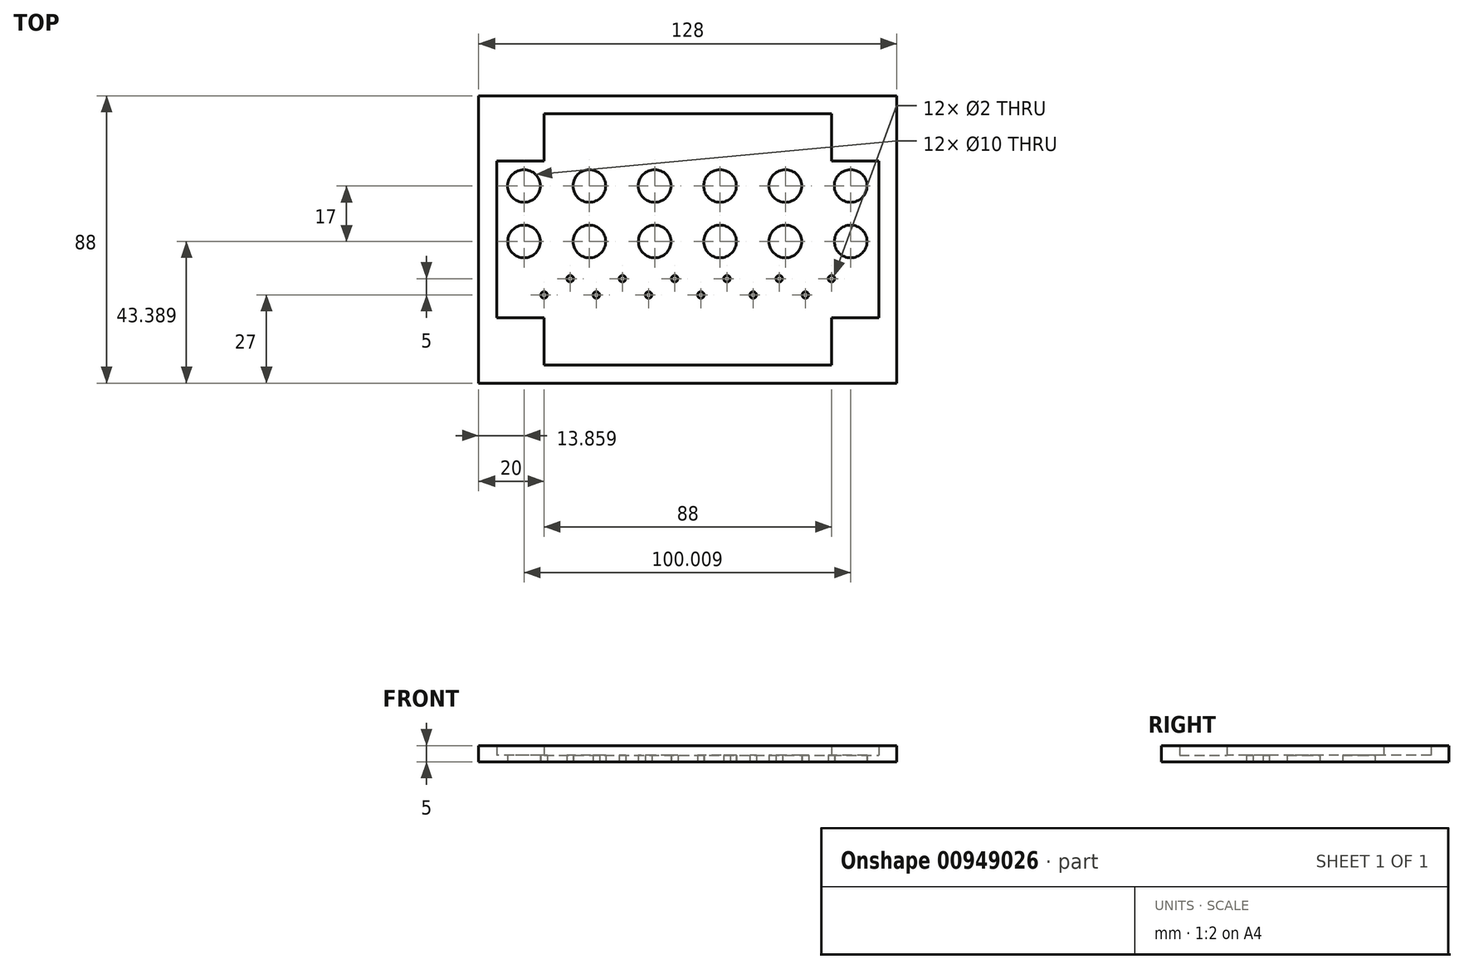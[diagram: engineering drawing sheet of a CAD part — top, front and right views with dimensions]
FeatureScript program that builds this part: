
annotation { "Feature Type Name" : "Feature", "Feature Type Description" : "" }
export const myFeature = defineFeature(function(context is Context, id is Id, definition is map)
    precondition{}
    {
        {
            var Q0;
            Q0=qCreatedBy(makeId("Top.planeOp"),FACE);
            var sketch = newSketch(context, id + "F0", { "sketchPlane" : qUnion([Q0])});
            skLineSegment(sketch, "E0.bottom", {"start": v(-64, 44) * mm, "end": v(64, 44) * mm});
            skLineSegment(sketch, "E0.top", {"start": v(-64, -44) * mm, "end": v(64, -44) * mm});
            skLineSegment(sketch, "E0.left", {"start": v(-64, 44) * mm, "end": v(-64, -44) * mm});
            skLineSegment(sketch, "E0.right", {"start": v(64, 44) * mm, "end": v(64, -44) * mm});
            skPoint(sketch, "E0.middle", {"position": v(0, 0) * mm});
            skLineSegment(sketch, "E1.bottom", {"start": v(-58.5, 38.5) * mm, "end": v(58.5, 38.5) * mm, "construction": true});
            skLineSegment(sketch, "E1.top", {"start": v(-58.5, -38.5) * mm, "end": v(58.5, -38.5) * mm, "construction": true});
            skLineSegment(sketch, "E1.left", {"start": v(-58.5, 38.5) * mm, "end": v(-58.5, -38.5) * mm, "construction": true});
            skLineSegment(sketch, "E1.right", {"start": v(58.5, 38.5) * mm, "end": v(58.5, -38.5) * mm, "construction": true});
            skLineSegment(sketch, "E2", {"start": v(44, 44) * mm, "end": v(44, 24) * mm, "construction": true});
            skLineSegment(sketch, "E3", {"start": v(44, 24) * mm, "end": v(64, 24) * mm, "construction": true});
            skLineSegment(sketch, "E4.MirrorCS", {"start": v(-44, 44) * mm, "end": v(-44, 24) * mm, "construction": true});
            skLineSegment(sketch, "E5.MirrorCS", {"start": v(-44, 24) * mm, "end": v(-64, 24) * mm, "construction": true});
            skLineSegment(sketch, "E6.MirrorCS", {"start": v(-44, -44) * mm, "end": v(-44, -24) * mm, "construction": true});
            skLineSegment(sketch, "E7.MirrorCS", {"start": v(-44, -24) * mm, "end": v(-64, -24) * mm, "construction": true});
            skLineSegment(sketch, "E8.MirrorCS", {"start": v(44, -44) * mm, "end": v(44, -24) * mm, "construction": true});
            skLineSegment(sketch, "E9.MirrorCS", {"start": v(44, -24) * mm, "end": v(64, -24) * mm, "construction": true});
            skLineSegment(sketch, "E10", {"start": v(-67.74, -17) * mm, "end": v(88.46, -17) * mm, "construction": true});
            skLineSegment(sketch, "E11", {"start": v(-79.12, -12) * mm, "end": v(91.25, -12) * mm, "construction": true});
            skCircle(sketch, "E12", {"center": v(4, -17) * mm, "radius": 1 * mm});
            skCircle(sketch, "E13", {"center": v(-4, -12) * mm, "radius": 1 * mm});
            skCircle(sketch, "E14.1.0.0", {"center": v(12, -12) * mm, "radius": 1 * mm});
            skCircle(sketch, "E14.2.0.0", {"center": v(28, -12) * mm, "radius": 1 * mm});
            skCircle(sketch, "E14.3.0.0", {"center": v(44, -12) * mm, "radius": 1 * mm});
            skLineSegment(sketch, "E14.direction1", {"start": v(-4, -12) * mm, "end": v(12, -12) * mm, "construction": true});
            skCircle(sketch, "E15.1.0.0", {"center": v(-20, -12) * mm, "radius": 1 * mm});
            skCircle(sketch, "E15.2.0.0", {"center": v(-36, -12) * mm, "radius": 1 * mm});
            skLineSegment(sketch, "E15.direction1", {"start": v(-4, -12) * mm, "end": v(-20, -12) * mm, "construction": true});
            skCircle(sketch, "E16.1.0.0", {"center": v(20, -17) * mm, "radius": 1 * mm});
            skCircle(sketch, "E16.2.0.0", {"center": v(36, -17) * mm, "radius": 1 * mm});
            skLineSegment(sketch, "E16.direction1", {"start": v(4, -17) * mm, "end": v(20, -17) * mm, "construction": true});
            skCircle(sketch, "E17.1.0.0", {"center": v(-12, -17) * mm, "radius": 1 * mm});
            skCircle(sketch, "E17.2.0.0", {"center": v(-28, -17) * mm, "radius": 1 * mm});
            skCircle(sketch, "E17.3.0.0", {"center": v(-44, -17) * mm, "radius": 1 * mm});
            skLineSegment(sketch, "E17.direction1", {"start": v(4, -17) * mm, "end": v(-12, -17) * mm, "construction": true});
            skCircle(sketch, "E18", {"center": v(-50.14, 16.39) * mm, "radius": 5 * mm});
            skCircle(sketch, "E19.0.1.0", {"center": v(-50.13, -0.61) * mm, "radius": 5 * mm});
            skCircle(sketch, "E19.1.0.0", {"center": v(-30.14, 16.39) * mm, "radius": 5 * mm});
            skCircle(sketch, "E19.1.1.0", {"center": v(-30.13, -0.61) * mm, "radius": 5 * mm});
            skCircle(sketch, "E19.2.0.0", {"center": v(-10.14, 16.39) * mm, "radius": 5 * mm});
            skCircle(sketch, "E19.2.1.0", {"center": v(-10.13, -0.61) * mm, "radius": 5 * mm});
            skCircle(sketch, "E19.3.0.0", {"center": v(9.86, 16.39) * mm, "radius": 5 * mm});
            skCircle(sketch, "E19.3.1.0", {"center": v(9.87, -0.61) * mm, "radius": 5 * mm});
            skCircle(sketch, "E19.4.0.0", {"center": v(29.86, 16.39) * mm, "radius": 5 * mm});
            skCircle(sketch, "E19.4.1.0", {"center": v(29.87, -0.61) * mm, "radius": 5 * mm});
            skCircle(sketch, "E19.5.0.0", {"center": v(49.86, 16.39) * mm, "radius": 5 * mm});
            skCircle(sketch, "E19.5.1.0", {"center": v(49.87, -0.61) * mm, "radius": 5 * mm});
            skLineSegment(sketch, "E19.direction1", {"start": v(-50.14, 16.39) * mm, "end": v(-30.14, 16.39) * mm, "construction": true});
            skLineSegment(sketch, "E19.direction2", {"start": v(-50.14, 16.39) * mm, "end": v(-50.13, -0.61) * mm, "construction": true});
            skSolve(sketch);
        }
        {
            var Q0;
            Q0 = qSketchRegion(id + "F0", true);
            extrude(context, id + "F1", {"entities" : qUnion([Q0]), "depth" : 2 * mm, "offsetDistance" : 25 * mm});
        }
        {
            var Q0;
            Q0=makeQuery(id+"F1.opExtrude","CAP_FACE",FACE,{"disambiguationData":[OSD([sQuery(id+"F0.wireOp",EDGE,"E0.bottom"),sQuery(id+"F0.wireOp",EDGE,"E0.top"),sQuery(id+"F0.wireOp",EDGE,"E0.left"),sQuery(id+"F0.wireOp",EDGE,"E0.right"),sQuery(id+"F0.wireOp",EDGE,"E12"),sQuery(id+"F0.wireOp",EDGE,"E13"),sQuery(id+"F0.wireOp",EDGE,"E14.1.0.0"),sQuery(id+"F0.wireOp",EDGE,"E14.2.0.0"),sQuery(id+"F0.wireOp",EDGE,"E14.3.0.0"),sQuery(id+"F0.wireOp",EDGE,"E15.1.0.0"),sQuery(id+"F0.wireOp",EDGE,"E15.2.0.0"),sQuery(id+"F0.wireOp",EDGE,"E16.1.0.0"),sQuery(id+"F0.wireOp",EDGE,"E16.2.0.0"),sQuery(id+"F0.wireOp",EDGE,"E17.1.0.0"),sQuery(id+"F0.wireOp",EDGE,"E17.2.0.0"),sQuery(id+"F0.wireOp",EDGE,"E17.3.0.0"),sQuery(id+"F0.wireOp",EDGE,"E18"),sQuery(id+"F0.wireOp",EDGE,"E19.0.1.0"),sQuery(id+"F0.wireOp",EDGE,"E19.1.0.0"),sQuery(id+"F0.wireOp",EDGE,"E19.1.1.0"),sQuery(id+"F0.wireOp",EDGE,"E19.2.0.0"),sQuery(id+"F0.wireOp",EDGE,"E19.2.1.0"),sQuery(id+"F0.wireOp",EDGE,"E19.3.0.0"),sQuery(id+"F0.wireOp",EDGE,"E19.3.1.0"),sQuery(id+"F0.wireOp",EDGE,"E19.4.0.0"),sQuery(id+"F0.wireOp",EDGE,"E19.4.1.0"),sQuery(id+"F0.wireOp",EDGE,"E19.5.0.0"),sQuery(id+"F0.wireOp",EDGE,"E19.5.1.0")])],"isStart":false});
            var sketch = newSketch(context, id + "F2", { "sketchPlane" : qUnion([Q0])});
            skLineSegment(sketch, "E20.0", {"start": v(-44, 44) * mm, "end": v(-44, 24) * mm});
            skLineSegment(sketch, "E21.0", {"start": v(-44, 24) * mm, "end": v(-64, 24) * mm});
            skLineSegment(sketch, "E22.0", {"start": v(-58.5, 38.5) * mm, "end": v(-58.5, -38.5) * mm});
            skPoint(sketch, "E23.0", {"position": v(-54, -24) * mm});
            skLineSegment(sketch, "E24.0", {"start": v(-44, -44) * mm, "end": v(-44, -24) * mm});
            skLineSegment(sketch, "E25.0", {"start": v(-44, -24) * mm, "end": v(-64, -24) * mm});
            skPoint(sketch, "E26.0", {"position": v(54, -24) * mm});
            skLineSegment(sketch, "E27.0", {"start": v(44, -24) * mm, "end": v(64, -24) * mm});
            skPoint(sketch, "E28.0", {"position": v(44, -34) * mm});
            skLineSegment(sketch, "E29.0", {"start": v(44, -44) * mm, "end": v(44, -24) * mm});
            skLineSegment(sketch, "E30.0", {"start": v(44, 44) * mm, "end": v(44, 24) * mm});
            skLineSegment(sketch, "E31.0", {"start": v(44, 24) * mm, "end": v(64, 24) * mm});
            skLineSegment(sketch, "E32.0", {"start": v(-58.5, 38.5) * mm, "end": v(58.5, 38.5) * mm});
            skLineSegment(sketch, "E33.0", {"start": v(58.5, 38.5) * mm, "end": v(58.5, -38.5) * mm});
            skLineSegment(sketch, "E34.0", {"start": v(-58.5, -38.5) * mm, "end": v(58.5, -38.5) * mm});
            skLineSegment(sketch, "E35.0", {"start": v(-64, -44) * mm, "end": v(64, -44) * mm});
            skLineSegment(sketch, "E36.0", {"start": v(64, 44) * mm, "end": v(64, -44) * mm});
            skLineSegment(sketch, "E37.0", {"start": v(-64, 44) * mm, "end": v(64, 44) * mm});
            skLineSegment(sketch, "E38.0", {"start": v(-64, 44) * mm, "end": v(-64, -44) * mm});
            skSolve(sketch);
        }
        {
            var Q0;
            {var subQ0=sQuery(id+"F2.wireOp",EDGE,"E37.0");var subQ1=sQuery(id+"F2.wireOp",EDGE,"E20.0");var subQ2=makeQuery(id+"F2.imprint","INTERSECT",VERTEX,{"derivedFrom":[subQ1,subQ0]});Q0=makeQuery(id+"F2.imprint","IMPRINT",FACE,{"disambiguationData":[TD([[makeQuery(id+"F2.imprint","IMPRINT",EDGE,{"disambiguationData":[TD([[subQ2,-1.0]])],"derivedFrom":subQ1}),1.0]])]});}
            var Q1;
            {var subQ3=sQuery(id+"F2.wireOp",EDGE,"E20.0");var subQ8=sQuery(id+"F2.wireOp",EDGE,"E37.0");var subQ11=makeQuery(id+"F2.imprint","INTERSECT",VERTEX,{"derivedFrom":[subQ3,subQ8]});Q1=makeQuery(id+"F2.imprint","IMPRINT",FACE,{"disambiguationData":[TD([[makeQuery(id+"F2.imprint","IMPRINT",EDGE,{"disambiguationData":[TD([[subQ11,-1.0]])],"derivedFrom":subQ3}),-1.0]])]});}
            var Q2;
            {var subQ0=sQuery(id+"F2.wireOp",EDGE,"E21.0");var subQ1=sQuery(id+"F2.wireOp",EDGE,"E20.0");var subQ2=makeQuery(id+"F2.imprint","INTERSECT",VERTEX,{"derivedFrom":[subQ1,subQ0]});Q2=makeQuery(id+"F2.imprint","IMPRINT",FACE,{"disambiguationData":[TD([[makeQuery(id+"F2.imprint","IMPRINT",EDGE,{"disambiguationData":[TD([[subQ2,1.0]])],"derivedFrom":subQ1}),-1.0]])]});}
            var Q3;
            {var subQ0=sQuery(id+"F2.wireOp",EDGE,"E38.0");var subQ1=sQuery(id+"F2.wireOp",EDGE,"E21.0");var subQ2=makeQuery(id+"F2.imprint","INTERSECT",VERTEX,{"derivedFrom":[subQ1,subQ0]});Q3=makeQuery(id+"F2.imprint","IMPRINT",FACE,{"disambiguationData":[TD([[makeQuery(id+"F2.imprint","IMPRINT",EDGE,{"disambiguationData":[TD([[subQ2,1.0]])],"derivedFrom":subQ1}),1.0]])]});}
            var Q4;
            {var subQ0=sQuery(id+"F2.wireOp",EDGE,"E34.0");var subQ1=sQuery(id+"F2.wireOp",EDGE,"E22.0");var subQ2=makeQuery(id+"F2.imprint","INTERSECT",VERTEX,{"derivedFrom":[subQ1,subQ0]});Q4=makeQuery(id+"F2.imprint","IMPRINT",FACE,{"disambiguationData":[TD([[makeQuery(id+"F2.imprint","IMPRINT",EDGE,{"disambiguationData":[TD([[subQ2,1.0]])],"derivedFrom":subQ1}),-1.0]])]});}
            var Q5;
            {var subQ0=sQuery(id+"F2.wireOp",EDGE,"E34.0");var subQ1=sQuery(id+"F2.wireOp",EDGE,"E22.0");var subQ2=makeQuery(id+"F2.imprint","INTERSECT",VERTEX,{"derivedFrom":[subQ1,subQ0]});Q5=makeQuery(id+"F2.imprint","IMPRINT",FACE,{"disambiguationData":[TD([[makeQuery(id+"F2.imprint","IMPRINT",EDGE,{"disambiguationData":[TD([[subQ2,1.0]])],"derivedFrom":subQ1}),1.0]])]});}
            var Q6;
            {var subQ0=sQuery(id+"F2.wireOp",EDGE,"E35.0");var subQ1=sQuery(id+"F2.wireOp",EDGE,"E24.0");var subQ2=makeQuery(id+"F2.imprint","INTERSECT",VERTEX,{"derivedFrom":[subQ1,subQ0]});Q6=makeQuery(id+"F2.imprint","IMPRINT",FACE,{"disambiguationData":[TD([[makeQuery(id+"F2.imprint","IMPRINT",EDGE,{"disambiguationData":[TD([[subQ2,-1.0]])],"derivedFrom":subQ1}),-1.0]])]});}
            var Q7;
            {var subQ3=sQuery(id+"F2.wireOp",EDGE,"E27.0");var subQ9=sQuery(id+"F2.wireOp",EDGE,"E36.0");var subQ10=makeQuery(id+"F2.imprint","INTERSECT",VERTEX,{"derivedFrom":[subQ3,subQ9]});Q7=makeQuery(id+"F2.imprint","IMPRINT",FACE,{"disambiguationData":[TD([[makeQuery(id+"F2.imprint","IMPRINT",EDGE,{"disambiguationData":[TD([[subQ10,1.0]])],"derivedFrom":subQ3}),-1.0]])]});}
            var Q8;
            {var subQ0=sQuery(id+"F2.wireOp",EDGE,"E29.0");var subQ1=sQuery(id+"F2.wireOp",EDGE,"E27.0");var subQ2=makeQuery(id+"F2.imprint","INTERSECT",VERTEX,{"derivedFrom":[subQ1,subQ0]});Q8=makeQuery(id+"F2.imprint","IMPRINT",FACE,{"disambiguationData":[TD([[makeQuery(id+"F2.imprint","IMPRINT",EDGE,{"disambiguationData":[TD([[subQ2,-1.0]])],"derivedFrom":subQ1}),-1.0]])]});}
            var Q9;
            {var subQ0=sQuery(id+"F2.wireOp",EDGE,"E36.0");var subQ1=sQuery(id+"F2.wireOp",EDGE,"E27.0");var subQ2=makeQuery(id+"F2.imprint","INTERSECT",VERTEX,{"derivedFrom":[subQ1,subQ0]});Q9=makeQuery(id+"F2.imprint","IMPRINT",FACE,{"disambiguationData":[TD([[makeQuery(id+"F2.imprint","IMPRINT",EDGE,{"disambiguationData":[TD([[subQ2,1.0]])],"derivedFrom":subQ1}),1.0]])]});}
            var Q10;
            {var subQ5=sQuery(id+"F2.wireOp",EDGE,"E30.0");var subQ9=sQuery(id+"F2.wireOp",EDGE,"E37.0");var subQ10=makeQuery(id+"F2.imprint","INTERSECT",VERTEX,{"derivedFrom":[subQ5,subQ9]});Q10=makeQuery(id+"F2.imprint","IMPRINT",FACE,{"disambiguationData":[TD([[makeQuery(id+"F2.imprint","IMPRINT",EDGE,{"disambiguationData":[TD([[subQ10,-1.0]])],"derivedFrom":subQ5}),1.0]])]});}
            var Q11;
            {var subQ0=sQuery(id+"F2.wireOp",EDGE,"E31.0");var subQ1=sQuery(id+"F2.wireOp",EDGE,"E30.0");var subQ2=makeQuery(id+"F2.imprint","INTERSECT",VERTEX,{"derivedFrom":[subQ1,subQ0]});Q11=makeQuery(id+"F2.imprint","IMPRINT",FACE,{"disambiguationData":[TD([[makeQuery(id+"F2.imprint","IMPRINT",EDGE,{"disambiguationData":[TD([[subQ2,1.0]])],"derivedFrom":subQ1}),1.0]])]});}
            extrude(context, id + "F3", {"entities" : qUnion([Q0, Q1, Q2, Q3, Q4, Q5, Q6, Q7, Q8, Q9, Q10, Q11]), "operationType" : NewBodyOperationType.ADD, "depth" : 3 * mm, "offsetDistance" : 25 * mm});
        }
    });
